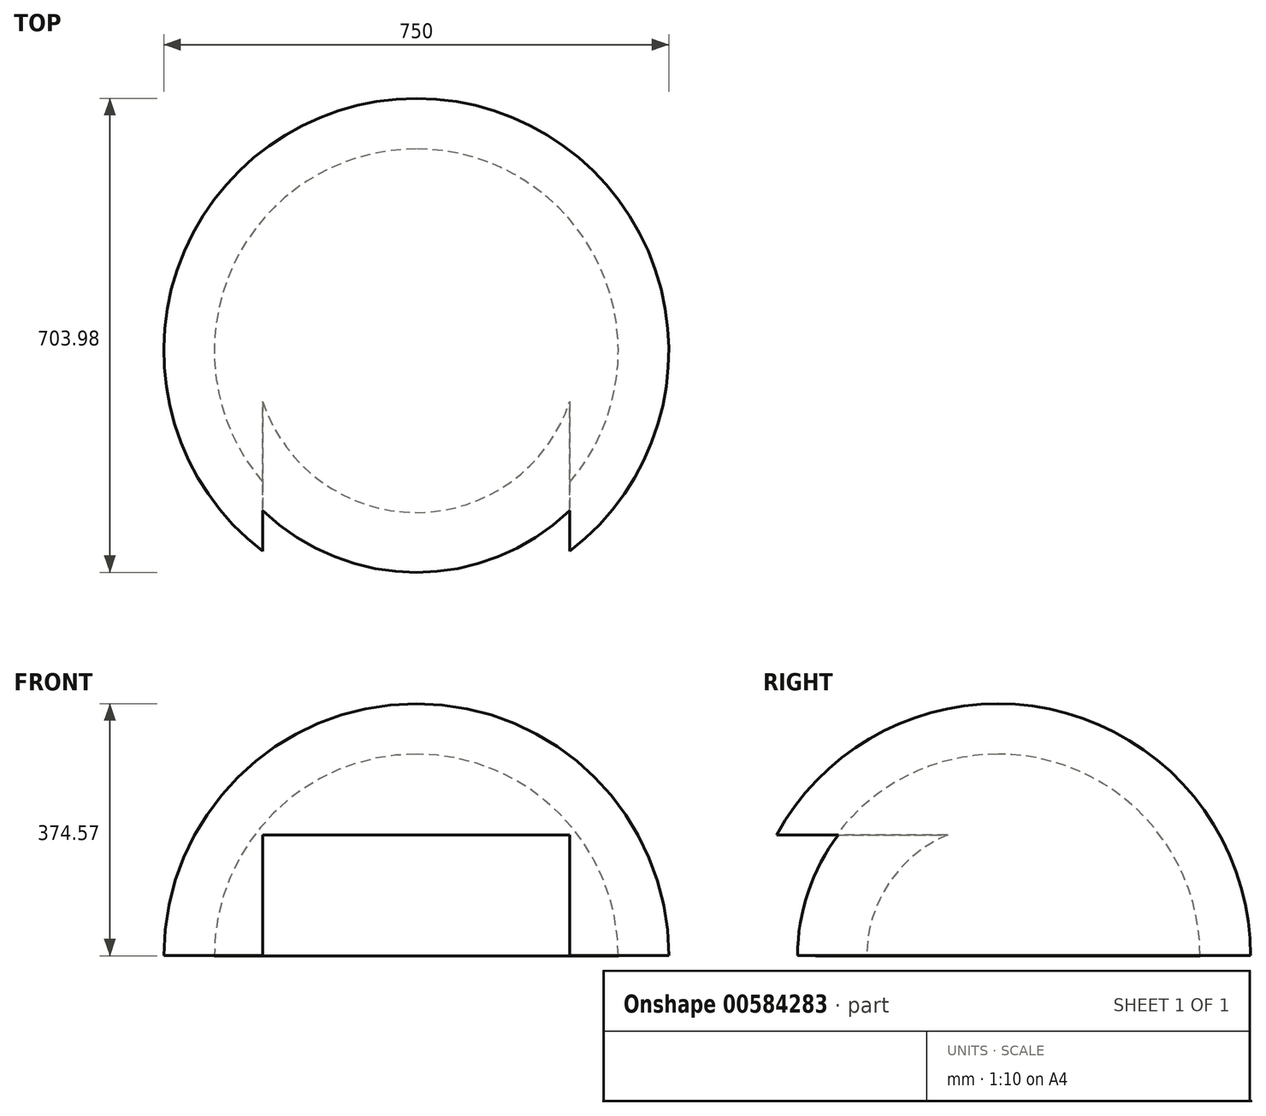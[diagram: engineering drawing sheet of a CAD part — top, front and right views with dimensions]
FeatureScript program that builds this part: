
annotation { "Feature Type Name" : "Feature", "Feature Type Description" : "" }
export const myFeature = defineFeature(function(context is Context, id is Id, definition is map)
    precondition{}
    {
        {
            var Q0;
            Q0=qCreatedBy(makeId("Right.planeOp"),FACE);
            var sketch = newSketch(context, id + "F0", { "sketchPlane" : qUnion([Q0])});
            skLineSegment(sketch, "E0", {"start": v(0, 300) * mm, "end": v(0, -300) * mm, "construction": true});
            skArc(sketch, "E1", {"start": v(0, 300) * mm, "mid": v(-211.98, 212.28) * mm, "end": v(-300, 0.43) * mm});
            skArc(sketch, "E2.0", {"start": v(0, 375) * mm, "mid": v(-264.98, 265.35) * mm, "end": v(-375, 0.53) * mm});
            skLineSegment(sketch, "E3", {"start": v(0, 375) * mm, "end": v(0, 300) * mm});
            skLineSegment(sketch, "E4", {"start": v(-375, 0.53) * mm, "end": v(-300, 0.43) * mm});
            skSolve(sketch);
        }
        {
            var Q0;
            Q0 = qSketchRegion(id + "F0", true);
            var Q1;
            Q1=sQuery(id+"F0.wireOp",EDGE,"E1");
            var Q2;
            Q2=sQuery(id+"F0.wireOp",EDGE,"E0");
            revolve(context, id + "F1", {"entities" : qUnion([Q0]), "surfaceEntities" : qUnion([Q1]), "axis" : qUnion([Q2]), "revolveType" : RevolveType.FULL});
        }
        {
            var Q0;
            Q0=qCreatedBy(makeId("Front.planeOp"),FACE);
            var sketch = newSketch(context, id + "F2", { "sketchPlane" : qUnion([Q0])});
            skLineSegment(sketch, "E5.bottom", {"start": v(228, 180) * mm, "end": v(-228, 180) * mm});
            skLineSegment(sketch, "E5.top", {"start": v(228, 0) * mm, "end": v(-228, 0) * mm});
            skLineSegment(sketch, "E5.left", {"start": v(228, 180) * mm, "end": v(228, 0) * mm});
            skLineSegment(sketch, "E5.right", {"start": v(-228, 180) * mm, "end": v(-228, 0) * mm});
            skPoint(sketch, "E5.middle", {"position": v(0, 90) * mm});
            skSolve(sketch);
        }
        {
            var Q0;
            Q0 = qSketchRegion(id + "F2", true);
            var Q1;
            Q1=sQuery(id+"F2.wireOp",EDGE,"E5.right");
            var Q2;
            Q2=sQuery(id+"F2.wireOp",EDGE,"E5.left");
            var Q3;
            Q3=sQuery(id+"F2.wireOp",EDGE,"E5.top");
            var Q4;
            Q4=sQuery(id+"F2.wireOp",EDGE,"E5.bottom");
            extrude(context, id + "F3", {"entities" : qUnion([Q0]), "operationType" : NewBodyOperationType.REMOVE, "surfaceEntities" : qUnion([Q1, Q2, Q3, Q4]), "depth" : 400 * mm, "offsetDistance" : 25 * mm});
        }
    });
